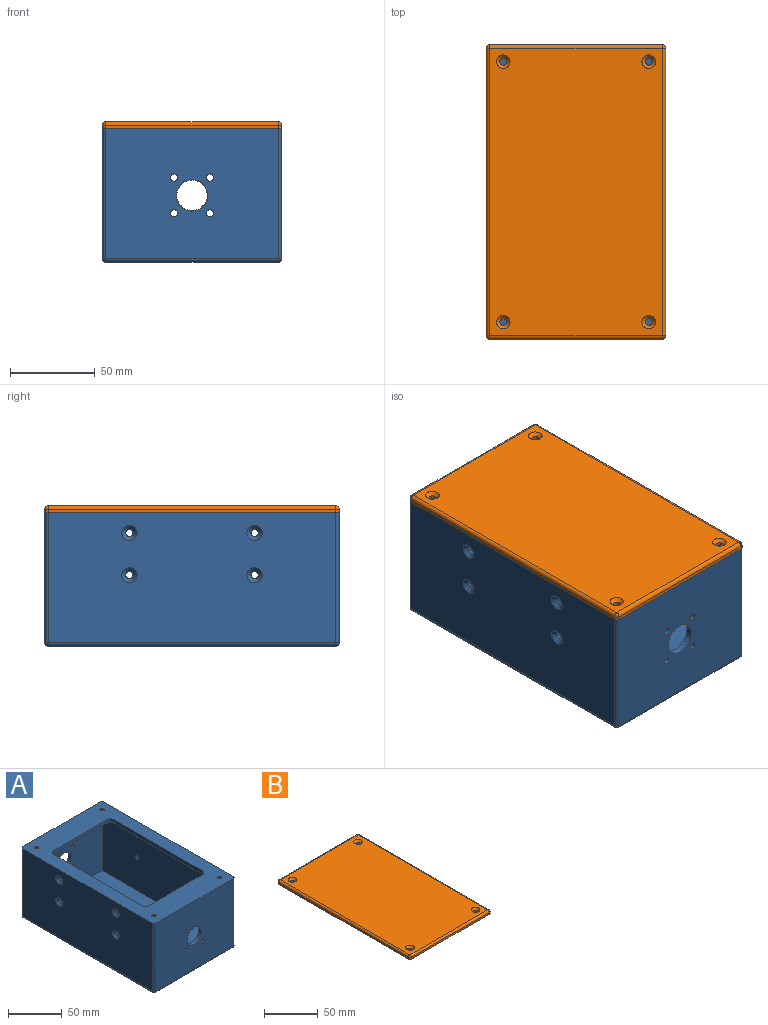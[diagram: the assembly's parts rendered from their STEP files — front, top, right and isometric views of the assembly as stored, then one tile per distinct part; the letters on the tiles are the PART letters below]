
ASSEMBLY  parts=2 mates=1
PART A: 62 faces, bbox 106x174x79 mm
  f0: plane 170x77mm, normal (-1,0,0), area 12835.5mm2, adj f13,f37,f39,f41,f43,f55,f58,f61
  f1: plane 170x102mm, normal (0,0,-1), area 17340mm2, adj f51,f56,f57,f61
  f2: plane 170x77mm, normal (1,0,0), area 12835.5mm2, adj f13,f21,f23,f25,f27,f50,f51,f52
  f3: plane 102x77mm, normal (0,-1,0), area 7512.4mm2, adj f13,f28,f29,f30,f31,f48,f50,f55
  f4: plane 102x77mm, normal (0,1,0), area 7541.4mm2, adj f13,f32,f33,f34,f35,f49,f52,f57
  f5: cylinder r=5mm len=5mm, axis (0,0,-1), area 31.4mm2, adj f6,f12,f13,f14
  f6: plane 69x4mm, normal (0,-1,0), area 276mm2, adj f5,f7,f13,f14
  f7: cylinder r=5mm len=5mm, axis (0,0,-1), area 31.4mm2, adj f6,f8,f13,f14
  f8: plane 115x4mm, normal (-1,0,0), area 460mm2, adj f7,f9,f13,f14
  f9: cylinder r=5mm len=5mm, axis (0,0,-1), area 31.4mm2, adj f8,f10,f13,f14
  f10: plane 69x4mm, normal (0,1,0), area 276mm2, adj f9,f11,f13,f14
  f11: cylinder r=5mm len=5mm, axis (0,0,-1), area 31.4mm2, adj f10,f12,f13,f14
  f12: plane 115x4mm, normal (1,0,0), area 460mm2, adj f5,f11,f13,f14
  f13: plane 174x106mm, normal (0,0,1), area 8534.2mm2, adj f0,f2,f3,f4,f5,f6,f7,f8
  f14: plane 166x98mm, normal (0,0,-1), area 6361.7mm2, adj f5,f6,f7,f8,f9,f10,f11,f12
  f15: plane 166x71mm, normal (1,0,0), area 11727.9mm2, adj f14,f16,f18,f19,f36,f38,f40,f42
  f16: plane 98x71mm, normal (0,1,0), area 6616.4mm2, adj f14,f15,f17,f19,f28,f29,f30,f31
  f17: plane 166x71mm, normal (-1,0,0), area 11727.9mm2, adj f14,f16,f18,f19,f20,f22,f24,f26
  f18: plane 98x71mm, normal (0,-1,0), area 6645.4mm2, adj f14,f15,f17,f19,f32,f33,f34,f35
  f19: plane 166x98mm, normal (0,0,1), area 16268mm2, adj f15,f16,f17,f18
  f20: cylinder r=2.15mm len=4.3mm, axis (1,0,0), area 22.3mm2, adj f17,f21
  f21: cone r=2.15mm half-angle=45deg, axis (1,0,0), area 69.4mm2, adj f2,f20
  f22: cylinder r=2.15mm len=4.3mm, axis (1,0,0), area 22.3mm2, adj f17,f23
  f23: cone r=2.15mm half-angle=45deg, axis (1,0,0), area 69.4mm2, adj f2,f22
  f24: cylinder r=2.15mm len=4.3mm, axis (1,0,0), area 22.3mm2, adj f17,f25
  f25: cone r=2.15mm half-angle=45deg, axis (1,0,0), area 69.4mm2, adj f2,f24
  f26: cylinder r=2.15mm len=4.3mm, axis (1,0,0), area 22.3mm2, adj f17,f27
  f27: cone r=2.15mm half-angle=45deg, axis (1,0,0), area 69.4mm2, adj f2,f26
  f28: cylinder r=2.15mm len=4.3mm, axis (0,-1,0), area 54mm2, adj f3,f16
  f29: cylinder r=2.15mm len=4.3mm, axis (0,-1,0), area 54mm2, adj f3,f16
  f30: cylinder r=2.15mm len=4.3mm, axis (0,-1,0), area 54mm2, adj f3,f16
  f31: cylinder r=2.15mm len=4.3mm, axis (0,-1,0), area 54mm2, adj f3,f16
  f32: cylinder r=2.15mm len=4.3mm, axis (0,1,0), area 54mm2, adj f4,f18
  f33: cylinder r=2.15mm len=4.3mm, axis (0,1,0), area 54mm2, adj f4,f18
  f34: cylinder r=2.15mm len=4.3mm, axis (0,1,0), area 54mm2, adj f4,f18
  f35: cylinder r=2.15mm len=4.3mm, axis (0,1,0), area 54mm2, adj f4,f18
  f36: cylinder r=2.15mm len=4.3mm, axis (-1,0,0), area 22.3mm2, adj f15,f37
  f37: cone r=2.15mm half-angle=45deg, axis (-1,0,0), area 69.4mm2, adj f0,f36
  f38: cylinder r=2.15mm len=4.3mm, axis (-1,0,0), area 22.3mm2, adj f15,f39
  f39: cone r=2.15mm half-angle=45deg, axis (-1,0,0), area 69.4mm2, adj f0,f38
  f40: cylinder r=2.15mm len=4.3mm, axis (-1,0,0), area 22.3mm2, adj f15,f41
  f41: cone r=2.15mm half-angle=45deg, axis (-1,0,0), area 69.4mm2, adj f0,f40
  f42: cylinder r=2.15mm len=4.3mm, axis (-1,0,0), area 22.3mm2, adj f15,f43
  f43: cone r=2.15mm half-angle=45deg, axis (-1,0,0), area 69.4mm2, adj f0,f42
  f44: cylinder r=2.05mm len=4.1mm, axis (0,0,1), area 51.5mm2, adj f13,f14
  f45: cylinder r=2.05mm len=4.1mm, axis (0,0,1), area 51.5mm2, adj f13,f14
  f46: cylinder r=2.05mm len=4.1mm, axis (0,0,1), area 51.5mm2, adj f13,f14
  f47: cylinder r=2.05mm len=4.1mm, axis (0,0,1), area 51.5mm2, adj f13,f14
  f48: cylinder r=9.5mm len=19mm, axis (0,-1,0), area 238.8mm2, adj f3,f16
  f49: cylinder r=9mm len=18mm, axis (0,1,0), area 226.2mm2, adj f4,f18
  f50: cylinder r=2mm len=77mm, axis (0,0,-1), area 241.9mm2, adj f2,f3,f13,f53
  f51: cylinder r=2mm len=170mm, axis (0,1,0), area 534.1mm2, adj f1,f2,f53,f54
  f52: cylinder r=2mm len=77mm, axis (0,0,1), area 241.9mm2, adj f2,f4,f13,f54
  f53: sphere r=2mm, area 6.3mm2, adj f50,f51,f56
  f54: sphere r=2mm, area 6.3mm2, adj f51,f52,f57
  f55: cylinder r=2mm len=77mm, axis (0,0,1), area 241.9mm2, adj f0,f3,f13,f59
  f56: cylinder r=2mm len=102mm, axis (-1,0,0), area 320.4mm2, adj f1,f3,f53,f59
  f57: cylinder r=2mm len=102mm, axis (1,0,0), area 320.4mm2, adj f1,f4,f54,f60
  f58: cylinder r=2mm len=77mm, axis (0,0,-1), area 241.9mm2, adj f0,f4,f13,f60
  f59: sphere r=2mm, area 6.3mm2, adj f55,f56,f61
  f60: sphere r=2mm, area 6.3mm2, adj f57,f58,f61
  f61: cylinder r=2mm len=170mm, axis (0,-1,0), area 534.1mm2, adj f0,f1,f59,f60
PART B: 26 faces, bbox 106x174x4 mm
  f0: plane 102x2mm, normal (0,1,0), area 204mm2, adj f5,f6,f10,f12
  f1: plane 170x2mm, normal (-1,0,0), area 340mm2, adj f5,f7,f12,f14
  f2: plane 102x2mm, normal (0,-1,0), area 204mm2, adj f5,f9,f14,f16
  f3: plane 170x2mm, normal (1,0,0), area 340mm2, adj f5,f8,f10,f16
  f4: plane 170x102mm, normal (0,0,1), area 17138.9mm2, adj f6,f7,f8,f9,f19,f21,f23,f25
  f5: plane 174x106mm, normal (0,0,-1), area 18387.8mm2, adj f0,f1,f2,f3,f10,f12,f14,f16
  f6: cylinder r=2mm len=102mm, axis (1,0,0), area 320.4mm2, adj f0,f4,f11,f13
  f7: cylinder r=2mm len=170mm, axis (0,1,0), area 534.1mm2, adj f1,f4,f13,f15
  f8: cylinder r=2mm len=170mm, axis (0,-1,0), area 534.1mm2, adj f3,f4,f11,f17
  f9: cylinder r=2mm len=102mm, axis (-1,0,0), area 320.4mm2, adj f2,f4,f15,f17
  f10: cylinder r=2mm len=2mm, axis (0,0,1), area 6.3mm2, adj f0,f3,f5,f11
  f11: sphere r=2mm, area 6.3mm2, adj f6,f8,f10
  f12: cylinder r=2mm len=2mm, axis (0,0,-1), area 6.3mm2, adj f0,f1,f5,f13
  f13: sphere r=2mm, area 6.3mm2, adj f6,f7,f12
  f14: cylinder r=2mm len=2mm, axis (0,0,1), area 6.3mm2, adj f1,f2,f5,f15
  f15: sphere r=2mm, area 6.3mm2, adj f7,f9,f14
  f16: cylinder r=2mm len=2mm, axis (0,0,-1), area 6.3mm2, adj f2,f3,f5,f17
  f17: sphere r=2mm, area 6.3mm2, adj f8,f9,f16
  f18: cylinder r=2.05mm len=4.1mm, axis (0,0,1), area 26.4mm2, adj f5,f19
  f19: cone r=2.05mm half-angle=45deg, axis (0,0,1), area 52.4mm2, adj f4,f18
  f20: cylinder r=2.05mm len=4.1mm, axis (0,0,1), area 26.4mm2, adj f5,f21
  f21: cone r=2.05mm half-angle=45deg, axis (0,0,1), area 52.4mm2, adj f4,f20
  f22: cylinder r=2.05mm len=4.1mm, axis (0,0,1), area 26.4mm2, adj f5,f23
  f23: cone r=2.05mm half-angle=45deg, axis (0,0,1), area 52.4mm2, adj f4,f22
  f24: cylinder r=2.05mm len=4.1mm, axis (0,0,1), area 26.4mm2, adj f5,f25
  f25: cone r=2.05mm half-angle=45deg, axis (0,0,1), area 52.4mm2, adj f4,f24
PLACE A t=(-2,2,0)mm
PLACE B t=(-2,-172,79)mm
MATE fastened B.f24 <-> A.f47  axis (0,0,-1) through (94,-162,79)mm
